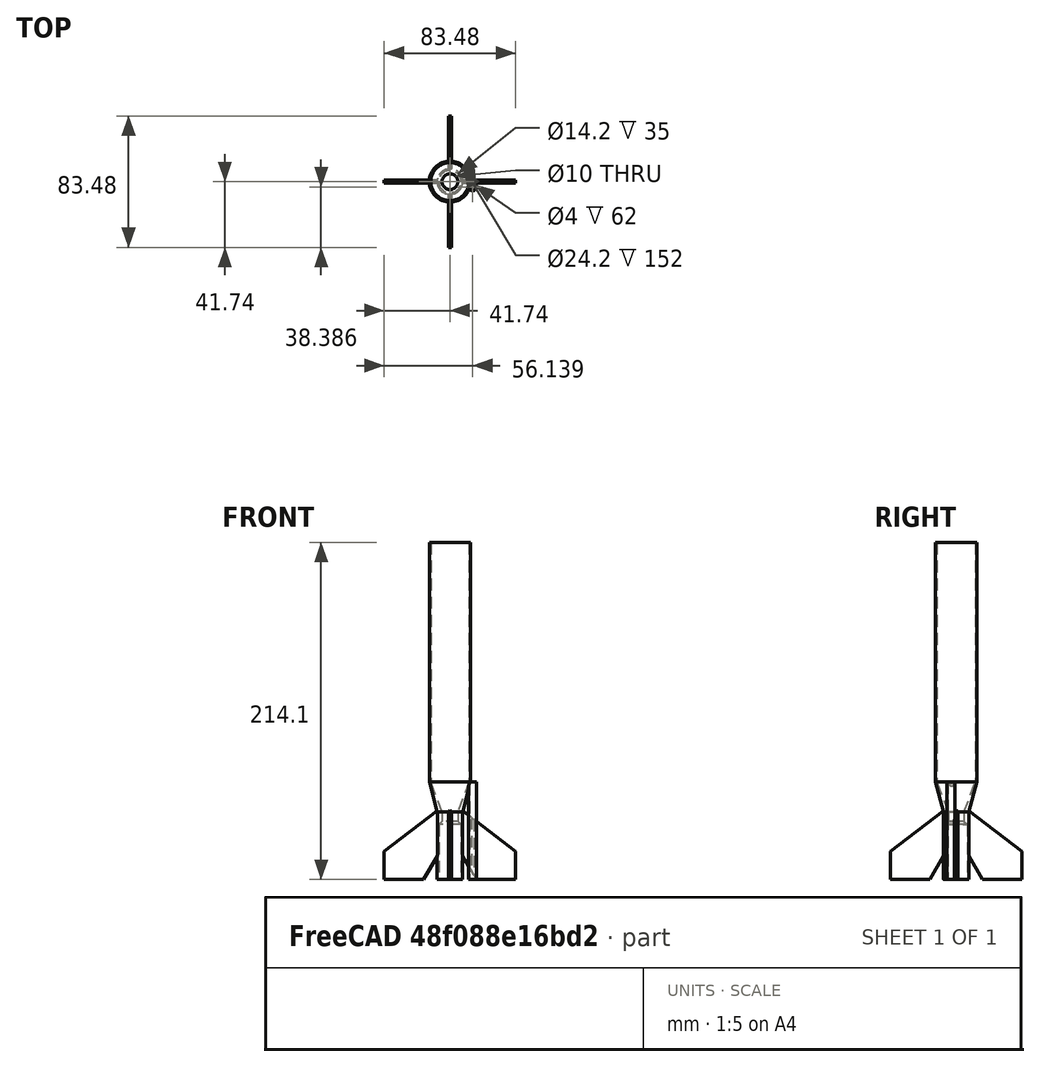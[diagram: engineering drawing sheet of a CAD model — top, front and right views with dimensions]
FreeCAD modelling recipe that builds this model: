
FCSTD DOCUMENT  (FreeCAD 0.20R29603 (Git))
Label: Ez3D-1350-4_FullLength
License: All rights reserved
LicenseURL: http://en.wikipedia.org/wiki/All_rights_reserved
objects: Sketcher::SketchObject×3, PartDesign::Pad×2, PartDesign::Revolution×1, PartDesign::PolarPattern×1, PartDesign::Body×1, Mesh::Feature×1
note: 11 computed .brp shape members not serialized (recipe doc carries the construction recipe); baked Part::Feature solids carry a one-line shape summary decoded from their .brp

FEATURE [Sketcher::SketchObject] Sketch  label="Fin Can and Transition"
  FullyConstrained = true
  MapMode = 5
  Placement = pos=(0,0,0) rot=(1,0,0;1.5708rad)
  Support = -> [XZ_Plane]
  sketch-geometry (10):
    g0: LineSegment StartX=7.1 StartY=0 StartZ=0 EndX=8.1 EndY=0 EndZ=0
    g1: LineSegment StartX=8.1 StartY=0 StartZ=0 EndX=8.1 EndY=43.1 EndZ=0
    g2: LineSegment StartX=5 StartY=43.1 StartZ=0 EndX=5 EndY=37.1 EndZ=0
    g3: LineSegment StartX=5 StartY=37.1 StartZ=0 EndX=7.1 EndY=35 EndZ=0
    g4: LineSegment StartX=7.1 StartY=35 StartZ=0 EndX=7.1 EndY=0 EndZ=0
    g5: LineSegment StartX=8.1 StartY=43.1 StartZ=0 EndX=13.1 EndY=62.1 EndZ=0
    g6: LineSegment StartX=12.1 StartY=214.1 StartZ=0 EndX=12.1 EndY=62.1 EndZ=0
    g7: LineSegment StartX=12.1 StartY=62.1 StartZ=0 EndX=5 EndY=43.1 EndZ=0
    g8: LineSegment StartX=13.1 StartY=62.1 StartZ=0 EndX=13.1 EndY=214.1 EndZ=0
    g9: LineSegment StartX=13.1 StartY=214.1 StartZ=0 EndX=12.1 EndY=214.1 EndZ=0
  constraints (30):
    c: PointOnObject(g0,g-1)
    c: PointOnObject(g0,g-1)
    c: Coincident(g0,g1)
    c: Vertical(g1)
    c: Vertical(g2)
    c: Coincident(g2,g3)
    c: Coincident(g3,g4)
    c: Coincident(g4,g0)
    c: Vertical(g4)
    c: DistanceX(g0,g0) = 1
    c: DistanceX(g-1,g0) = 7.1
    c: DistanceY(g0,g3) = 35
    c: Angle(g3) = -0.785398
    c: DistanceX(g-1,g2) = 5
    c: Coincident(g1,g5)
    c: Vertical(g6)
    c: Coincident(g6,g7)
    c: Coincident(g2,g7)
    c: Vertical(g8)
    c: Coincident(g8,g9)
    c: Coincident(g9,g6)
    c: Horizontal(g9)
    c: DistanceY(g2,g2) = 6
    c: DistanceY(g2,g6) = 19
    c: Horizontal(g6,g8)
    c: Horizontal(g2,g1)
    c: Coincident(g8,g5)
    c: DistanceY(g8,g8) = 152
    c: DistanceX(g-1,g6) = 12.1
    c: DistanceX(g9,g9) = 1
FEATURE [PartDesign::Revolution] Revolution  label="Revolution for Fin Can"
  Angle = 360
  Axis = (0,-2e-16,1)
  Base = (0,0,0)
  Placement = pos=(0,0,0) rot=(1,0,0;1.5708rad)
  Profile = -> Sketch
  ReferenceAxis = -> Sketch [V_Axis]
  Reversed = true
FEATURE [Sketcher::SketchObject] Sketch001  label="Fin"
  FullyConstrained = true
  MapMode = 5
  Placement = pos=(0,0,0) rot=(1,0,0;1.5708rad)
  Support = -> [XZ_Plane]
  sketch-geometry (5):
    g0: LineSegment StartX=16.7376 StartY=0 StartZ=0 EndX=41.7376 EndY=0 EndZ=0
    g1: LineSegment StartX=41.7376 StartY=0 StartZ=0 EndX=41.7376 EndY=18 EndZ=0
    g2: LineSegment StartX=41.7376 StartY=18 StartZ=0 EndX=7.5 EndY=44 EndZ=0
    g3: LineSegment StartX=7.5 StartY=44 StartZ=0 EndX=7.5 EndY=16 EndZ=0
    g4: LineSegment StartX=7.5 StartY=16 StartZ=0 EndX=16.7376 EndY=0 EndZ=0
  constraints (15):
    c: Horizontal(g0)
    c: Coincident(g0,g1)
    c: Coincident(g1,g2)
    c: Vertical(g1)
    c: Coincident(g2,g3)
    c: Vertical(g3)
    c: Coincident(g3,g4)
    c: Coincident(g0,g4)
    c: DistanceX(g-1,g2) = 7.5
    c: Angle(g4) = -1.0472
    c: PointOnObject(g0,g-1)
    c: DistanceY(g1,g1) = 18
    c: DistanceX(g0,g0) = 25
    c: DistanceY(g3,g3) = 28
    c: DistanceY(g0,g2) = 44
FEATURE [PartDesign::Pad] Pad  label="Fin 2mm thick"
  BaseFeature = -> Revolution
  Direction = (0,-1,-2e-16)
  Length = 2
  Length2 = 100
  Midplane = true
  Placement = pos=(0,0,0) rot=(1,0,0;1.5708rad)
  Profile = -> Sketch001
  Type = 0
FEATURE [PartDesign::PolarPattern] PolarPattern  label="Add Multiple Fins"
  Angle = 360
  Axis = -> Z_Axis
  BaseFeature = -> Pad
  Occurrences = 4
  Originals = -> [Pad]
  Placement = pos=(0,0,0) rot=(1,0,0;1.5708rad)
FEATURE [Sketcher::SketchObject] Sketch002  label="Launch Lug 4mm ID 5mm OD"
  FullyConstrained = false
  MapMode = 5
  Support = -> [XY_Plane]
  sketch-geometry (2):
    g0: Circle CenterX=14.3994 CenterY=-3.35421 CenterZ=0 NormalX=0 NormalY=0 NormalZ=1 AngleXU=0 Radius=2.5
    g1: Circle CenterX=14.3994 CenterY=-3.35421 CenterZ=0 NormalX=0 NormalY=0 NormalZ=1 AngleXU=0 Radius=2
  constraints (3):
    c: Coincident(g1,g0)
    c: Diameter(g0) = 5
    c: Diameter(g1) = 4
FEATURE [PartDesign::Pad] Pad001  label="Launch Lug 62mm long"
  BaseFeature = -> PolarPattern
  Direction = (0,0,1)
  Length = 62
  Length2 = 100
  Placement = pos=(0,0,0) rot=(1,0,0;1.5708rad)
  Profile = -> Sketch002
  Type = 0
FEATURE [PartDesign::Body] Body
  Group = -> [Sketch,Revolution,Sketch001,Pad,PolarPattern,Sketch002,Pad001]
  Origin = -> Origin
  Tip = -> Pad001
FEATURE [Mesh::Feature] _3mmThread20x2_5_5mmTall  label="13mmThread20x2.5-5mmTall"
